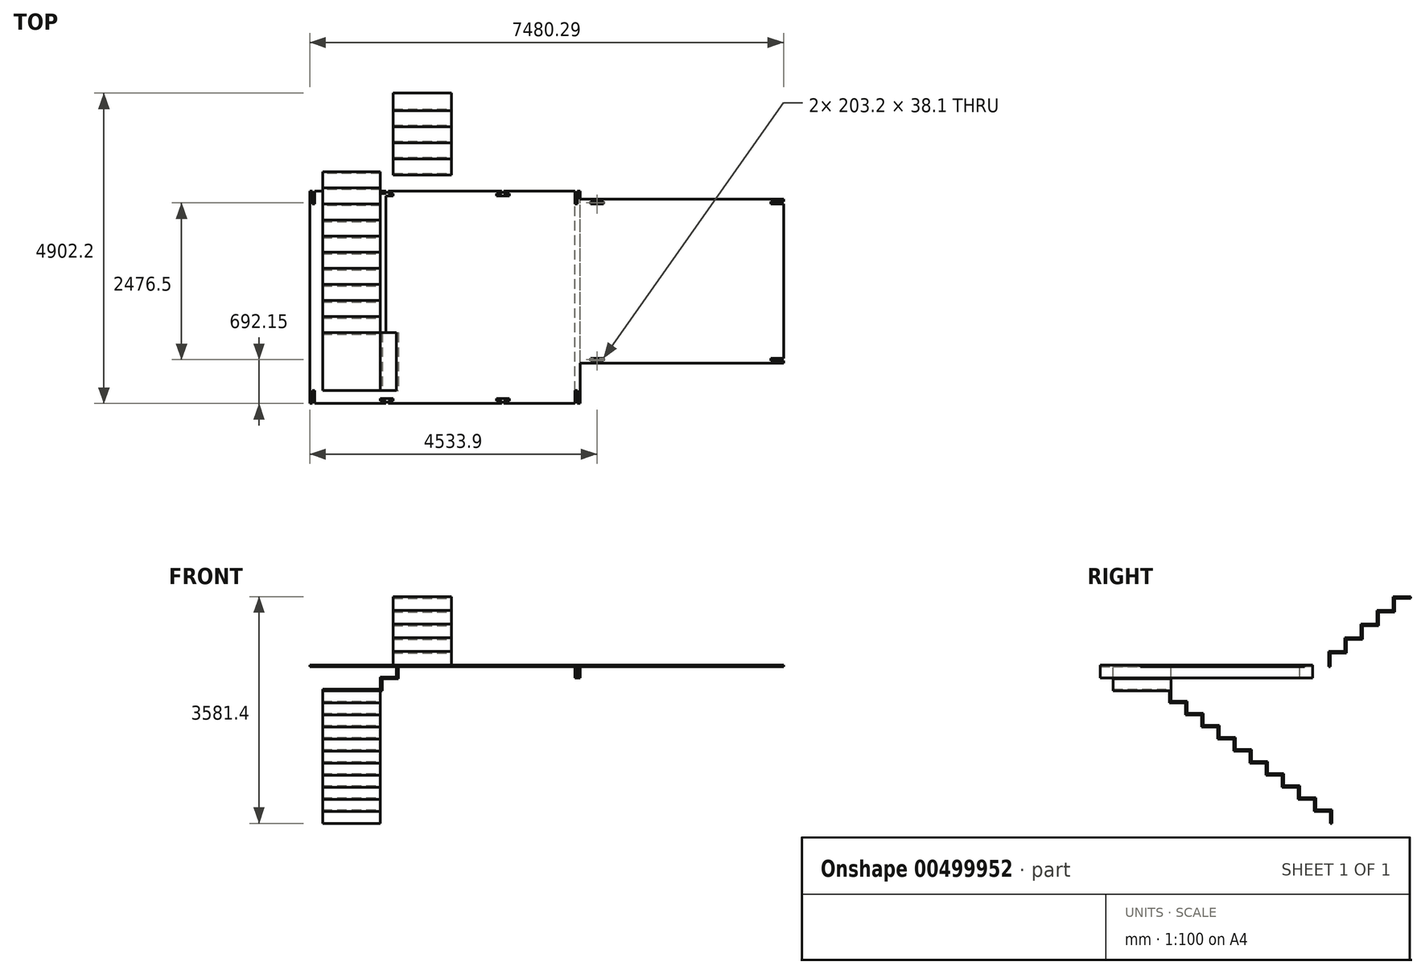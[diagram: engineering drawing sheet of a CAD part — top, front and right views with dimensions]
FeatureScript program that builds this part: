
annotation { "Feature Type Name" : "Feature", "Feature Type Description" : "" }
export const myFeature = defineFeature(function(context is Context, id is Id, definition is map)
    precondition{}
    {
        {
            var Q0;
            Q0=qCreatedBy(makeId("Top.planeOp"),FACE);
            var sketch = newSketch(context, id + "F0", { "sketchPlane" : qUnion([Q0])});
            skLineSegment(sketch, "E0.bottom", {"start": v(-4114.17, 1676.4) * mm, "end": v(4114.16, 1676.4) * mm});
            skLineSegment(sketch, "E0.top", {"start": v(-4114.17, -1676.4) * mm, "end": v(4114.17, -1676.4) * mm});
            skLineSegment(sketch, "E0.left", {"start": v(-4114.17, 1676.4) * mm, "end": v(-4114.17, -1676.4) * mm});
            skPoint(sketch, "E0.middle", {"position": v(0, 0) * mm});
            skLineSegment(sketch, "E1.bottom", {"start": v(-4076.07, -1676.4) * mm, "end": v(-4037.97, -1676.4) * mm});
            skLineSegment(sketch, "E1.top", {"start": v(-4076.07, -1473.2) * mm, "end": v(-4037.97, -1473.2) * mm});
            skLineSegment(sketch, "E1.left", {"start": v(-4076.07, -1676.4) * mm, "end": v(-4076.07, -1473.2) * mm});
            skLineSegment(sketch, "E1.right", {"start": v(-4037.97, -1676.4) * mm, "end": v(-4037.97, -1473.2) * mm});
            skLineSegment(sketch, "E2.bottom", {"start": v(-2914.02, -1676.4) * mm, "end": v(-2875.92, -1676.4) * mm});
            skLineSegment(sketch, "E2.top", {"start": v(-2914.02, -1473.2) * mm, "end": v(-2875.92, -1473.2) * mm});
            skLineSegment(sketch, "E2.left", {"start": v(-2914.02, -1676.4) * mm, "end": v(-2914.02, -1473.2) * mm});
            skLineSegment(sketch, "E2.right", {"start": v(-2875.92, -1676.4) * mm, "end": v(-2875.92, -1473.2) * mm});
            skLineSegment(sketch, "E3.bottom", {"start": v(-1085.22, -1676.4) * mm, "end": v(-1047.12, -1676.4) * mm});
            skLineSegment(sketch, "E3.top", {"start": v(-1085.22, -1473.2) * mm, "end": v(-1047.12, -1473.2) * mm});
            skLineSegment(sketch, "E3.left", {"start": v(-1085.22, -1676.4) * mm, "end": v(-1085.22, -1473.2) * mm});
            skLineSegment(sketch, "E3.right", {"start": v(-1047.12, -1676.4) * mm, "end": v(-1047.12, -1473.2) * mm});
            skLineSegment(sketch, "E4.bottom", {"start": v(76.84, -1676.4) * mm, "end": v(114.94, -1676.4) * mm});
            skLineSegment(sketch, "E4.top", {"start": v(76.84, -1473.2) * mm, "end": v(114.94, -1473.2) * mm});
            skLineSegment(sketch, "E4.left", {"start": v(76.84, -1676.4) * mm, "end": v(76.84, -1473.2) * mm});
            skLineSegment(sketch, "E4.right", {"start": v(114.94, -1676.4) * mm, "end": v(114.94, -1473.2) * mm});
            skLineSegment(sketch, "E5.bottom", {"start": v(-4076.07, 1676.4) * mm, "end": v(-4037.97, 1676.4) * mm});
            skLineSegment(sketch, "E5.top", {"start": v(-4076.07, 1473.2) * mm, "end": v(-4037.97, 1473.2) * mm});
            skLineSegment(sketch, "E5.left", {"start": v(-4076.07, 1676.4) * mm, "end": v(-4076.07, 1473.2) * mm});
            skLineSegment(sketch, "E5.right", {"start": v(-4037.97, 1676.4) * mm, "end": v(-4037.97, 1473.2) * mm});
            skLineSegment(sketch, "E6.bottom", {"start": v(-2914.02, 1676.4) * mm, "end": v(-2875.92, 1676.4) * mm});
            skLineSegment(sketch, "E6.top", {"start": v(-2914.02, 1473.2) * mm, "end": v(-2875.92, 1473.2) * mm});
            skLineSegment(sketch, "E6.left", {"start": v(-2914.02, 1676.4) * mm, "end": v(-2914.02, 1473.2) * mm});
            skLineSegment(sketch, "E6.right", {"start": v(-2875.92, 1676.4) * mm, "end": v(-2875.92, 1473.2) * mm});
            skLineSegment(sketch, "E7.bottom", {"start": v(-1085.22, 1676.4) * mm, "end": v(-1047.12, 1676.4) * mm});
            skLineSegment(sketch, "E7.top", {"start": v(-1085.22, 1473.2) * mm, "end": v(-1047.12, 1473.2) * mm});
            skLineSegment(sketch, "E7.left", {"start": v(-1085.22, 1676.4) * mm, "end": v(-1085.22, 1473.2) * mm});
            skLineSegment(sketch, "E7.right", {"start": v(-1047.12, 1676.4) * mm, "end": v(-1047.12, 1473.2) * mm});
            skLineSegment(sketch, "E8.bottom", {"start": v(76.84, 1676.4) * mm, "end": v(114.94, 1676.4) * mm});
            skLineSegment(sketch, "E8.top", {"start": v(76.84, 1473.2) * mm, "end": v(114.94, 1473.2) * mm});
            skLineSegment(sketch, "E8.left", {"start": v(76.84, 1676.4) * mm, "end": v(76.84, 1473.2) * mm});
            skLineSegment(sketch, "E8.right", {"start": v(114.94, 1676.4) * mm, "end": v(114.94, 1473.2) * mm});
            skLineSegment(sketch, "E9.bottom", {"start": v(76.84, -1676.4) * mm, "end": v(153.04, -1676.4) * mm});
            skLineSegment(sketch, "E9.top", {"start": v(76.84, 1676.4) * mm, "end": v(153.04, 1676.4) * mm});
            skLineSegment(sketch, "E9.left", {"start": v(76.84, -1676.4) * mm, "end": v(76.84, 1676.4) * mm});
            skLineSegment(sketch, "E9.right", {"start": v(153.04, -1676.4) * mm, "end": v(153.04, 1676.4) * mm});
            skLineSegment(sketch, "E10", {"start": v(-4076.07, -1638.3) * mm, "end": v(-4037.97, -1638.3) * mm});
            skLineSegment(sketch, "E11", {"start": v(-4076.07, 1638.3) * mm, "end": v(-4037.97, 1638.3) * mm});
            skLineSegment(sketch, "E12", {"start": v(76.84, -1638.3) * mm, "end": v(114.94, -1638.3) * mm});
            skLineSegment(sketch, "E13.bottom", {"start": v(-1167.77, -1638.3) * mm, "end": v(-964.57, -1638.3) * mm});
            skLineSegment(sketch, "E13.top", {"start": v(-1167.77, -1600.2) * mm, "end": v(-964.57, -1600.2) * mm});
            skLineSegment(sketch, "E13.left", {"start": v(-1167.77, -1638.3) * mm, "end": v(-1167.77, -1600.2) * mm});
            skLineSegment(sketch, "E13.right", {"start": v(-964.57, -1638.3) * mm, "end": v(-964.57, -1600.2) * mm});
            skLineSegment(sketch, "E14.bottom", {"start": v(-2996.57, 1676.4) * mm, "end": v(-3910.97, 1676.4) * mm});
            skLineSegment(sketch, "E14.top", {"start": v(-2996.57, -1473.2) * mm, "end": v(-3910.96, -1473.2) * mm});
            skLineSegment(sketch, "E14.left", {"start": v(-2996.57, 1676.4) * mm, "end": v(-2996.57, -1473.2) * mm});
            skLineSegment(sketch, "E14.right", {"start": v(-3910.97, 1676.4) * mm, "end": v(-3910.96, -1473.2) * mm});
            skPoint(sketch, "E15.oppositeSnap0", {"position": v(-2875.92, -1574.8) * mm});
            skLineSegment(sketch, "E15.bottom", {"start": v(-2996.57, -1638.3) * mm, "end": v(-2793.37, -1638.3) * mm});
            skLineSegment(sketch, "E15.top", {"start": v(-2996.57, -1600.2) * mm, "end": v(-2793.37, -1600.2) * mm});
            skLineSegment(sketch, "E15.left", {"start": v(-2996.57, -1638.3) * mm, "end": v(-2996.57, -1600.2) * mm});
            skLineSegment(sketch, "E15.right", {"start": v(-2793.37, -1638.3) * mm, "end": v(-2793.37, -1600.2) * mm});
            skLineSegment(sketch, "E16.bottom", {"start": v(-2996.57, 1638.3) * mm, "end": v(-2793.37, 1638.3) * mm});
            skLineSegment(sketch, "E16.top", {"start": v(-2996.57, 1600.2) * mm, "end": v(-2793.37, 1600.2) * mm});
            skLineSegment(sketch, "E16.left", {"start": v(-2996.57, 1638.3) * mm, "end": v(-2996.57, 1600.2) * mm});
            skLineSegment(sketch, "E16.right", {"start": v(-2793.37, 1638.3) * mm, "end": v(-2793.37, 1600.2) * mm});
            skLineSegment(sketch, "E17.bottom", {"start": v(-1167.77, 1638.3) * mm, "end": v(-964.57, 1638.3) * mm});
            skLineSegment(sketch, "E17.top", {"start": v(-1167.77, 1600.2) * mm, "end": v(-964.57, 1600.2) * mm});
            skLineSegment(sketch, "E17.left", {"start": v(-1167.77, 1638.3) * mm, "end": v(-1167.77, 1600.2) * mm});
            skLineSegment(sketch, "E17.right", {"start": v(-964.57, 1638.3) * mm, "end": v(-964.57, 1600.2) * mm});
            skLineSegment(sketch, "E18.bottom", {"start": v(-2996.57, -1473.2) * mm, "end": v(-2742.57, -1473.2) * mm});
            skLineSegment(sketch, "E18.top", {"start": v(-2996.57, -558.8) * mm, "end": v(-2742.56, -558.8) * mm});
            skLineSegment(sketch, "E18.left", {"start": v(-2996.57, -1473.2) * mm, "end": v(-2996.57, -558.8) * mm});
            skLineSegment(sketch, "E18.right", {"start": v(-2742.57, -1473.2) * mm, "end": v(-2742.57, -558.8) * mm});
            skLineSegment(sketch, "E19.bottom", {"start": v(-2742.56, -558.8) * mm, "end": v(-2717.16, -558.8) * mm});
            skLineSegment(sketch, "E19.top", {"start": v(-2742.57, -1473.2) * mm, "end": v(-2717.17, -1473.2) * mm});
            skLineSegment(sketch, "E19.left", {"start": v(-2742.57, -558.8) * mm, "end": v(-2742.57, -1473.2) * mm});
            skLineSegment(sketch, "E19.right", {"start": v(-2717.17, -558.8) * mm, "end": v(-2717.17, -1473.2) * mm});
            skLineSegment(sketch, "E20.bottom", {"start": v(-2996.57, -558.8) * mm, "end": v(-2914.02, -558.8) * mm});
            skLineSegment(sketch, "E20.top", {"start": v(-2996.57, 1676.4) * mm, "end": v(-2914.02, 1676.4) * mm});
            skLineSegment(sketch, "E20.left", {"start": v(-2996.57, -558.8) * mm, "end": v(-2996.57, 1676.4) * mm});
            skLineSegment(sketch, "E20.right", {"start": v(-2914.02, -558.8) * mm, "end": v(-2914.02, 1676.4) * mm});
            skLineSegment(sketch, "E21.bottom", {"start": v(-2793.37, 1676.4) * mm, "end": v(-1878.97, 1676.4) * mm});
            skLineSegment(sketch, "E21.top", {"start": v(-2793.37, 1955.8) * mm, "end": v(-1878.97, 1955.8) * mm});
            skLineSegment(sketch, "E21.left", {"start": v(-2793.37, 1676.4) * mm, "end": v(-2793.37, 1955.8) * mm});
            skLineSegment(sketch, "E21.right", {"start": v(-1878.97, 1676.4) * mm, "end": v(-1878.97, 1955.8) * mm});
            skLineSegment(sketch, "E22.bottom", {"start": v(153.04, 1549.4) * mm, "end": v(3366.14, 1549.4) * mm});
            skLineSegment(sketch, "E22.top", {"start": v(153.04, -1041.4) * mm, "end": v(3366.13, -1041.4) * mm});
            skLineSegment(sketch, "E22.left", {"start": v(153.04, 1549.4) * mm, "end": v(153.04, -1041.4) * mm});
            skLineSegment(sketch, "E22.right", {"start": v(3366.14, 1549.4) * mm, "end": v(3366.14, -1041.4) * mm});
            skLineSegment(sketch, "E23.bottom", {"start": v(318.14, 1511.3) * mm, "end": v(521.34, 1511.3) * mm});
            skLineSegment(sketch, "E23.top", {"start": v(318.14, 1473.2) * mm, "end": v(521.34, 1473.2) * mm});
            skLineSegment(sketch, "E23.left", {"start": v(318.14, 1511.3) * mm, "end": v(318.14, 1473.2) * mm});
            skLineSegment(sketch, "E23.right", {"start": v(521.34, 1511.3) * mm, "end": v(521.34, 1473.2) * mm});
            skLineSegment(sketch, "E24.bottom", {"start": v(318.14, -965.2) * mm, "end": v(521.34, -965.2) * mm});
            skLineSegment(sketch, "E24.top", {"start": v(318.14, -1003.3) * mm, "end": v(521.34, -1003.3) * mm});
            skLineSegment(sketch, "E24.left", {"start": v(318.14, -965.2) * mm, "end": v(318.14, -1003.3) * mm});
            skLineSegment(sketch, "E24.right", {"start": v(521.34, -965.2) * mm, "end": v(521.34, -1003.3) * mm});
            skLineSegment(sketch, "E25.bottom", {"start": v(3366.14, -965.2) * mm, "end": v(3162.94, -965.2) * mm});
            skLineSegment(sketch, "E25.top", {"start": v(3366.14, -1003.3) * mm, "end": v(3162.94, -1003.3) * mm});
            skLineSegment(sketch, "E25.left", {"start": v(3366.14, -965.2) * mm, "end": v(3366.14, -1003.3) * mm});
            skLineSegment(sketch, "E25.right", {"start": v(3162.94, -965.2) * mm, "end": v(3162.94, -1003.3) * mm});
            skLineSegment(sketch, "E26.bottom", {"start": v(3366.14, 1511.3) * mm, "end": v(3162.94, 1511.3) * mm});
            skLineSegment(sketch, "E26.top", {"start": v(3366.14, 1473.2) * mm, "end": v(3162.94, 1473.2) * mm});
            skLineSegment(sketch, "E26.left", {"start": v(3366.14, 1511.3) * mm, "end": v(3366.14, 1473.2) * mm});
            skLineSegment(sketch, "E26.right", {"start": v(3162.94, 1511.3) * mm, "end": v(3162.94, 1473.2) * mm});
            skSolve(sketch);
        }
        {
            var Q0;
            Q0=makeQuery(id+"F0.imprint","IMPRINT",FACE,{"disambiguationData":[TD([[makeQuery(id+"F0.imprint","IMPRINT",EDGE,{"derivedFrom":sQuery(id+"F0.wireOp",EDGE,"E1.bottom")}),1.0]])]});
            var Q1;
            Q1=makeQuery(id+"F0.imprint","IMPRINT",FACE,{"disambiguationData":[TD([[makeQuery(id+"F0.imprint","IMPRINT",EDGE,{"derivedFrom":sQuery(id+"F0.wireOp",EDGE,"E2.bottom")}),1.0]])]});
            var Q2;
            Q2=makeQuery(id+"F0.imprint","IMPRINT",FACE,{"disambiguationData":[TD([[makeQuery(id+"F0.imprint","IMPRINT",EDGE,{"derivedFrom":sQuery(id+"F0.wireOp",EDGE,"E3.bottom")}),1.0]])]});
            var Q3;
            Q3=makeQuery(id+"F0.imprint","IMPRINT",FACE,{"disambiguationData":[TD([[makeQuery(id+"F0.imprint","IMPRINT",EDGE,{"derivedFrom":sQuery(id+"F0.wireOp",EDGE,"E4.bottom")}),1.0]])]});
            var Q4;
            Q4=makeQuery(id+"F0.imprint","IMPRINT",FACE,{"disambiguationData":[TD([[makeQuery(id+"F0.imprint","IMPRINT",EDGE,{"derivedFrom":sQuery(id+"F0.wireOp",EDGE,"E5.bottom")}),-1.0]])]});
            var Q5;
            Q5=makeQuery(id+"F0.imprint","IMPRINT",FACE,{"disambiguationData":[TD([[makeQuery(id+"F0.imprint","IMPRINT",EDGE,{"derivedFrom":sQuery(id+"F0.wireOp",EDGE,"E6.bottom")}),-1.0]])]});
            var Q6;
            Q6=makeQuery(id+"F0.imprint","IMPRINT",FACE,{"disambiguationData":[TD([[makeQuery(id+"F0.imprint","IMPRINT",EDGE,{"derivedFrom":sQuery(id+"F0.wireOp",EDGE,"E7.bottom")}),-1.0]])]});
            var Q7;
            Q7=makeQuery(id+"F0.imprint","IMPRINT",FACE,{"disambiguationData":[TD([[makeQuery(id+"F0.imprint","IMPRINT",EDGE,{"derivedFrom":sQuery(id+"F0.wireOp",EDGE,"E8.bottom")}),-1.0]])]});
            var Q8;
            {var subQ4=sQuery(id+"F0.wireOp",EDGE,"E0.left");Q8=makeQuery(id+"F0.imprint","IMPRINT",FACE,{"disambiguationData":[TD([[makeQuery(id+"F0.imprint","IMPRINT",EDGE,{"derivedFrom":subQ4}),1.0]])]});}
            var Q9;
            Q9=makeQuery(id+"F0.imprint","IMPRINT",FACE,{"disambiguationData":[TD([[makeQuery(id+"F0.imprint","IMPRINT",EDGE,{"derivedFrom":sQuery(id+"F0.wireOp",EDGE,"E9.bottom")}),1.0]])]});
            var Q10;
            {var subQ0=sQuery(id+"F0.wireOp",EDGE,"E3.top");Q10=makeQuery(id+"F0.imprint","IMPRINT",FACE,{"disambiguationData":[TD([[makeQuery(id+"F0.imprint","IMPRINT",EDGE,{"derivedFrom":subQ0}),-1.0]])]});}
            var Q11;
            {var subQ2=sQuery(id+"F0.wireOp",EDGE,"E4.top");Q11=makeQuery(id+"F0.imprint","IMPRINT",FACE,{"disambiguationData":[TD([[makeQuery(id+"F0.imprint","IMPRINT",EDGE,{"derivedFrom":subQ2}),1.0]])]});}
            var Q12;
            {var subQ0=sQuery(id+"F0.wireOp",EDGE,"E7.top");Q12=makeQuery(id+"F0.imprint","IMPRINT",FACE,{"disambiguationData":[TD([[makeQuery(id+"F0.imprint","IMPRINT",EDGE,{"derivedFrom":subQ0}),1.0]])]});}
            var Q13;
            {var subQ0=sQuery(id+"F0.wireOp",EDGE,"E6.top");Q13=makeQuery(id+"F0.imprint","IMPRINT",FACE,{"disambiguationData":[TD([[makeQuery(id+"F0.imprint","IMPRINT",EDGE,{"derivedFrom":subQ0}),1.0]])]});}
            var Q14;
            {var subQ0=sQuery(id+"F0.wireOp",EDGE,"E2.top");Q14=makeQuery(id+"F0.imprint","IMPRINT",FACE,{"disambiguationData":[TD([[makeQuery(id+"F0.imprint","IMPRINT",EDGE,{"derivedFrom":subQ0}),-1.0]])]});}
            var Q15;
            {var subQ0=sQuery(id+"F0.wireOp",EDGE,"E6.left");var subQ5=sQuery(id+"F0.wireOp",EDGE,"E16.bottom");var subQ7=makeQuery(id+"F0.imprint","INTERSECT",VERTEX,{"derivedFrom":[subQ0,subQ5]});Q15=makeQuery(id+"F0.imprint","IMPRINT",FACE,{"disambiguationData":[TD([[makeQuery(id+"F0.imprint","IMPRINT",EDGE,{"disambiguationData":[TD([[subQ7,1.0]])],"derivedFrom":subQ0}),-1.0]])]});}
            var Q16;
            {var subQ38=sQuery(id+"F0.wireOp",EDGE,"E3.top");Q16=makeQuery(id+"F0.imprint","IMPRINT",FACE,{"disambiguationData":[TD([[makeQuery(id+"F0.imprint","IMPRINT",EDGE,{"derivedFrom":subQ38}),1.0]])]});}
            var Q17;
            {var subQ0=sQuery(id+"F0.wireOp",EDGE,"E18.bottom");var subQ1=sQuery(id+"F0.wireOp",EDGE,"E2.left");var subQ2=makeQuery(id+"F0.imprint","INTERSECT",VERTEX,{"derivedFrom":[subQ1,subQ0]});Q17=makeQuery(id+"F0.imprint","IMPRINT",FACE,{"disambiguationData":[TD([[makeQuery(id+"F0.imprint","IMPRINT",EDGE,{"disambiguationData":[TD([[subQ2,1.0]])],"derivedFrom":subQ1}),-1.0]])]});}
            var Q18;
            Q18=makeQuery(id+"F0.imprint","IMPRINT",FACE,{"disambiguationData":[TD([[makeQuery(id+"F0.imprint","IMPRINT",EDGE,{"derivedFrom":sQuery(id+"F0.wireOp",EDGE,"E19.bottom")}),-1.0]])]});
            var Q19;
            {var subQ3=sQuery(id+"F0.wireOp",EDGE,"E20.bottom");Q19=makeQuery(id+"F0.imprint","IMPRINT",FACE,{"disambiguationData":[TD([[makeQuery(id+"F0.imprint","IMPRINT",EDGE,{"derivedFrom":subQ3}),1.0]])]});}
            var Q20;
            {var subQ5=sQuery(id+"F0.wireOp",EDGE,"E20.top");Q20=makeQuery(id+"F0.imprint","IMPRINT",FACE,{"disambiguationData":[TD([[makeQuery(id+"F0.imprint","IMPRINT",EDGE,{"derivedFrom":subQ5}),-1.0]])]});}
            var Q21;
            Q21=makeQuery(id+"F0.imprint","IMPRINT",FACE,{"disambiguationData":[TD([[makeQuery(id+"F0.imprint","IMPRINT",EDGE,{"derivedFrom":sQuery(id+"F0.wireOp",EDGE,"E21.bottom")}),1.0]])]});
            var Q22;
            Q22=makeQuery(id+"F0.imprint","IMPRINT",FACE,{"disambiguationData":[TD([[makeQuery(id+"F0.imprint","IMPRINT",EDGE,{"derivedFrom":sQuery(id+"F0.wireOp",EDGE,"E22.bottom")}),-1.0]])]});
            extrude(context, id + "F1", {"entities" : qUnion([Q0, Q1, Q2, Q3, Q4, Q5, Q6, Q7, Q8, Q9, Q10, Q11, Q12, Q13, Q14, Q15, Q16, Q17, Q18, Q19, Q20, Q21, Q22]), "oppositeDirection" : true, "depth" : 25.4 * mm, "offsetDistance" : 25.4 * mm});
        }
        {
            var Q0;
            {var subQ1=sQuery(id+"F0.wireOp",EDGE,"E8.top");Q0=makeQuery(id+"F0.imprint","IMPRINT",FACE,{"disambiguationData":[TD([[makeQuery(id+"F0.imprint","IMPRINT",EDGE,{"derivedFrom":subQ1}),-1.0]])]});}
            extrude(context, id + "F2", {"entities" : qUnion([Q0]), "operationType" : NewBodyOperationType.ADD, "oppositeDirection" : true, "depth" : 203.2 * mm, "offsetDistance" : 25.4 * mm});
        }
        {
            var Q0;
            Q0=makeQuery(id+"F0.imprint","IMPRINT",FACE,{"disambiguationData":[TD([[makeQuery(id+"F0.imprint","IMPRINT",EDGE,{"derivedFrom":sQuery(id+"F0.wireOp",EDGE,"E19.bottom")}),-1.0]])]});
            extrude(context, id + "F3", {"entities" : qUnion([Q0]), "operationType" : NewBodyOperationType.ADD, "oppositeDirection" : true, "depth" : 215.9 * mm, "offsetDistance" : 25.4 * mm});
        }
        {
            var Q0;
            Q0=makeQuery(id+"F3.opExtrude","SWEPT_FACE",FACE,{"disambiguationData":[OSD([sQuery(id+"F0.wireOp",EDGE,"E19.right")])]});
            var sketch = newSketch(context, id + "F4", { "sketchPlane" : qUnion([Q0])});
            skLineSegment(sketch, "E27.bottom", {"start": v(-1473.2, -215.9) * mm, "end": v(-558.8, -215.9) * mm});
            skLineSegment(sketch, "E27.top", {"start": v(-1473.2, -190.5) * mm, "end": v(-558.8, -190.5) * mm});
            skLineSegment(sketch, "E27.left", {"start": v(-1473.2, -215.9) * mm, "end": v(-1473.2, -190.5) * mm});
            skLineSegment(sketch, "E27.right", {"start": v(-558.8, -215.9) * mm, "end": v(-558.8, -190.5) * mm});
            skSolve(sketch);
        }
        {
            var Q0;
            Q0 = qSketchRegion(id + "F4", true);
            extrude(context, id + "F5", {"entities" : qUnion([Q0]), "operationType" : NewBodyOperationType.ADD, "oppositeDirection" : true, "depth" : 279.4 * mm, "offsetDistance" : 25.4 * mm});
        }
        {
            var Q0;
            Q0=makeQuery(id+"F5.opExtrude","SWEPT_FACE",FACE,{"disambiguationData":[OSD([sQuery(id+"F4.wireOp",EDGE,"E27.top")])]});
            var sketch = newSketch(context, id + "F6", { "sketchPlane" : qUnion([Q0])});
            skLineSegment(sketch, "E28.bottom", {"start": v(-2996.57, -558.8) * mm, "end": v(-2971.17, -558.8) * mm});
            skLineSegment(sketch, "E28.top", {"start": v(-2996.57, -1473.2) * mm, "end": v(-2971.17, -1473.2) * mm});
            skLineSegment(sketch, "E28.left", {"start": v(-2996.57, -558.8) * mm, "end": v(-2996.57, -1473.2) * mm});
            skLineSegment(sketch, "E28.right", {"start": v(-2971.17, -558.8) * mm, "end": v(-2971.17, -1473.2) * mm});
            skSolve(sketch);
        }
        {
            var Q0;
            Q0 = qSketchRegion(id + "F6", true);
            extrude(context, id + "F7", {"entities" : qUnion([Q0]), "operationType" : NewBodyOperationType.ADD, "oppositeDirection" : true, "depth" : 215.9 * mm, "offsetDistance" : 25.4 * mm});
        }
        {
            var Q0;
            Q0=makeQuery(id+"F7.opExtrude","SWEPT_FACE",FACE,{"disambiguationData":[OSD([sQuery(id+"F6.wireOp",EDGE,"E28.right")])]});
            var sketch = newSketch(context, id + "F8", { "sketchPlane" : qUnion([Q0])});
            skLineSegment(sketch, "E29.bottom", {"start": v(-1473.2, -406.4) * mm, "end": v(-558.8, -406.4) * mm});
            skLineSegment(sketch, "E29.top", {"start": v(-1473.2, -381) * mm, "end": v(-558.8, -381) * mm});
            skLineSegment(sketch, "E29.left", {"start": v(-1473.2, -406.4) * mm, "end": v(-1473.2, -381) * mm});
            skLineSegment(sketch, "E29.right", {"start": v(-558.8, -406.4) * mm, "end": v(-558.8, -381) * mm});
            skSolve(sketch);
        }
        {
            var Q0;
            Q0 = qSketchRegion(id + "F8", true);
            extrude(context, id + "F9", {"entities" : qUnion([Q0]), "operationType" : NewBodyOperationType.ADD, "oppositeDirection" : true, "depth" : 939.8 * mm, "offsetDistance" : 25.4 * mm});
        }
        {
            var Q0;
            Q0=makeQuery(id+"F9.opExtrude","SWEPT_FACE",FACE,{"disambiguationData":[OSD([sQuery(id+"F8.wireOp",EDGE,"E29.top")])]});
            var sketch = newSketch(context, id + "F10", { "sketchPlane" : qUnion([Q0])});
            skLineSegment(sketch, "E30.bottom", {"start": v(-3910.97, -558.8) * mm, "end": v(-2996.57, -558.8) * mm});
            skLineSegment(sketch, "E30.top", {"start": v(-3910.97, -584.2) * mm, "end": v(-2996.57, -584.2) * mm});
            skLineSegment(sketch, "E30.left", {"start": v(-3910.97, -558.8) * mm, "end": v(-3910.97, -584.2) * mm});
            skLineSegment(sketch, "E30.right", {"start": v(-2996.57, -558.8) * mm, "end": v(-2996.57, -584.2) * mm});
            skSolve(sketch);
        }
        {
            var Q0;
            Q0 = qSketchRegion(id + "F10", true);
            extrude(context, id + "F11", {"entities" : qUnion([Q0]), "operationType" : NewBodyOperationType.ADD, "oppositeDirection" : true, "depth" : 215.9 * mm, "offsetDistance" : 25.4 * mm});
        }
        {
            var Q0;
            Q0=makeQuery(id+"F11.opExtrude","SWEPT_FACE",FACE,{"disambiguationData":[OSD([sQuery(id+"F10.wireOp",EDGE,"E30.top")])]});
            var sketch = newSketch(context, id + "F12", { "sketchPlane" : qUnion([Q0])});
            skLineSegment(sketch, "E31.bottom", {"start": v(-3910.97, -596.9) * mm, "end": v(-2996.57, -596.9) * mm});
            skLineSegment(sketch, "E31.top", {"start": v(-3910.97, -571.5) * mm, "end": v(-2996.57, -571.5) * mm});
            skLineSegment(sketch, "E31.left", {"start": v(-3910.97, -596.9) * mm, "end": v(-3910.97, -571.5) * mm});
            skLineSegment(sketch, "E31.right", {"start": v(-2996.57, -596.9) * mm, "end": v(-2996.57, -571.5) * mm});
            skSolve(sketch);
        }
        {
            var Q0;
            Q0 = qSketchRegion(id + "F12", true);
            extrude(context, id + "F13", {"entities" : qUnion([Q0]), "operationType" : NewBodyOperationType.ADD, "oppositeDirection" : true, "depth" : 279.4 * mm, "offsetDistance" : 25.4 * mm});
        }
        {
            var Q0;
            Q0=makeQuery(id+"F13.opExtrude","SWEPT_FACE",FACE,{"disambiguationData":[OSD([sQuery(id+"F12.wireOp",EDGE,"E31.top")])]});
            var sketch = newSketch(context, id + "F14", { "sketchPlane" : qUnion([Q0])});
            skLineSegment(sketch, "E32.bottom", {"start": v(-3910.97, -304.8) * mm, "end": v(-2996.57, -304.8) * mm});
            skLineSegment(sketch, "E32.top", {"start": v(-3910.97, -330.2) * mm, "end": v(-2996.57, -330.2) * mm});
            skLineSegment(sketch, "E32.left", {"start": v(-3910.97, -304.8) * mm, "end": v(-3910.97, -330.2) * mm});
            skLineSegment(sketch, "E32.right", {"start": v(-2996.57, -304.8) * mm, "end": v(-2996.57, -330.2) * mm});
            skSolve(sketch);
        }
        {
            var Q0;
            Q0 = qSketchRegion(id + "F14", true);
            extrude(context, id + "F15", {"entities" : qUnion([Q0]), "operationType" : NewBodyOperationType.ADD, "oppositeDirection" : true, "depth" : 215.9 * mm, "offsetDistance" : 25.4 * mm});
        }
        {
            var Q0;
            Q0=makeQuery(id+"F15.opExtrude","SWEPT_FACE",FACE,{"disambiguationData":[OSD([sQuery(id+"F14.wireOp",EDGE,"E32.top")])]});
            var sketch = newSketch(context, id + "F16", { "sketchPlane" : qUnion([Q0])});
            skLineSegment(sketch, "E33.bottom", {"start": v(-3910.97, -787.4) * mm, "end": v(-2996.57, -787.4) * mm});
            skLineSegment(sketch, "E33.top", {"start": v(-3910.97, -762) * mm, "end": v(-2996.57, -762) * mm});
            skLineSegment(sketch, "E33.left", {"start": v(-3910.97, -787.4) * mm, "end": v(-3910.97, -762) * mm});
            skLineSegment(sketch, "E33.right", {"start": v(-2996.57, -787.4) * mm, "end": v(-2996.57, -762) * mm});
            skSolve(sketch);
        }
        {
            var Q0;
            Q0 = qSketchRegion(id + "F16", true);
            extrude(context, id + "F17", {"entities" : qUnion([Q0]), "operationType" : NewBodyOperationType.ADD, "oppositeDirection" : true, "depth" : 279.4 * mm, "offsetDistance" : 25.4 * mm});
        }
        {
            var Q0;
            Q0=makeQuery(id+"F17.opExtrude","SWEPT_FACE",FACE,{"disambiguationData":[OSD([sQuery(id+"F16.wireOp",EDGE,"E33.top")])]});
            var sketch = newSketch(context, id + "F18", { "sketchPlane" : qUnion([Q0])});
            skLineSegment(sketch, "E34.bottom", {"start": v(-3910.97, -50.8) * mm, "end": v(-2996.57, -50.8) * mm});
            skLineSegment(sketch, "E34.top", {"start": v(-3910.97, -76.2) * mm, "end": v(-2996.57, -76.2) * mm});
            skLineSegment(sketch, "E34.left", {"start": v(-3910.97, -50.8) * mm, "end": v(-3910.97, -76.2) * mm});
            skLineSegment(sketch, "E34.right", {"start": v(-2996.57, -50.8) * mm, "end": v(-2996.57, -76.2) * mm});
            skSolve(sketch);
        }
        {
            var Q0;
            Q0 = qSketchRegion(id + "F18", true);
            extrude(context, id + "F19", {"entities" : qUnion([Q0]), "operationType" : NewBodyOperationType.ADD, "oppositeDirection" : true, "depth" : 215.9 * mm, "offsetDistance" : 25.4 * mm});
        }
        {
            var Q0;
            Q0=makeQuery(id+"F19.opExtrude","SWEPT_FACE",FACE,{"disambiguationData":[OSD([sQuery(id+"F18.wireOp",EDGE,"E34.top")])]});
            var sketch = newSketch(context, id + "F20", { "sketchPlane" : qUnion([Q0])});
            skLineSegment(sketch, "E35.bottom", {"start": v(-3910.97, -977.9) * mm, "end": v(-2996.57, -977.9) * mm});
            skLineSegment(sketch, "E35.top", {"start": v(-3910.97, -952.5) * mm, "end": v(-2996.57, -952.5) * mm});
            skLineSegment(sketch, "E35.left", {"start": v(-3910.97, -977.9) * mm, "end": v(-3910.97, -952.5) * mm});
            skLineSegment(sketch, "E35.right", {"start": v(-2996.57, -977.9) * mm, "end": v(-2996.57, -952.5) * mm});
            skSolve(sketch);
        }
        {
            var Q0;
            Q0 = qSketchRegion(id + "F20", true);
            extrude(context, id + "F21", {"entities" : qUnion([Q0]), "operationType" : NewBodyOperationType.ADD, "oppositeDirection" : true, "depth" : 279.4 * mm, "offsetDistance" : 25.4 * mm});
        }
        {
            var Q0;
            Q0=makeQuery(id+"F21.opExtrude","SWEPT_FACE",FACE,{"disambiguationData":[OSD([sQuery(id+"F20.wireOp",EDGE,"E35.top")])]});
            var sketch = newSketch(context, id + "F22", { "sketchPlane" : qUnion([Q0])});
            skLineSegment(sketch, "E36.bottom", {"start": v(-3910.97, 203.2) * mm, "end": v(-2996.57, 203.2) * mm});
            skLineSegment(sketch, "E36.top", {"start": v(-3910.97, 177.8) * mm, "end": v(-2996.57, 177.8) * mm});
            skLineSegment(sketch, "E36.left", {"start": v(-3910.97, 203.2) * mm, "end": v(-3910.97, 177.8) * mm});
            skLineSegment(sketch, "E36.right", {"start": v(-2996.57, 203.2) * mm, "end": v(-2996.57, 177.8) * mm});
            skSolve(sketch);
        }
        {
            var Q0;
            Q0 = qSketchRegion(id + "F22", true);
            extrude(context, id + "F23", {"entities" : qUnion([Q0]), "operationType" : NewBodyOperationType.ADD, "oppositeDirection" : true, "depth" : 215.9 * mm, "offsetDistance" : 25.4 * mm});
        }
        {
            var Q0;
            Q0=makeQuery(id+"F23.opExtrude","SWEPT_FACE",FACE,{"disambiguationData":[OSD([sQuery(id+"F22.wireOp",EDGE,"E36.top")])]});
            var sketch = newSketch(context, id + "F24", { "sketchPlane" : qUnion([Q0])});
            skLineSegment(sketch, "E37.bottom", {"start": v(-3910.97, -1168.4) * mm, "end": v(-2996.57, -1168.4) * mm});
            skLineSegment(sketch, "E37.top", {"start": v(-3910.97, -1143) * mm, "end": v(-2996.57, -1143) * mm});
            skLineSegment(sketch, "E37.left", {"start": v(-3910.97, -1168.4) * mm, "end": v(-3910.97, -1143) * mm});
            skLineSegment(sketch, "E37.right", {"start": v(-2996.57, -1168.4) * mm, "end": v(-2996.57, -1143) * mm});
            skSolve(sketch);
        }
        {
            var Q0;
            Q0 = qSketchRegion(id + "F24", true);
            extrude(context, id + "F25", {"entities" : qUnion([Q0]), "operationType" : NewBodyOperationType.ADD, "oppositeDirection" : true, "depth" : 279.4 * mm, "offsetDistance" : 25.4 * mm});
        }
        {
            var Q0;
            Q0=makeQuery(id+"F25.opExtrude","SWEPT_FACE",FACE,{"disambiguationData":[OSD([sQuery(id+"F24.wireOp",EDGE,"E37.top")])]});
            var sketch = newSketch(context, id + "F26", { "sketchPlane" : qUnion([Q0])});
            skLineSegment(sketch, "E38.bottom", {"start": v(-3910.97, 457.2) * mm, "end": v(-2996.57, 457.2) * mm});
            skLineSegment(sketch, "E38.top", {"start": v(-3910.97, 431.8) * mm, "end": v(-2996.57, 431.8) * mm});
            skLineSegment(sketch, "E38.left", {"start": v(-3910.97, 457.2) * mm, "end": v(-3910.97, 431.8) * mm});
            skLineSegment(sketch, "E38.right", {"start": v(-2996.57, 457.2) * mm, "end": v(-2996.57, 431.8) * mm});
            skSolve(sketch);
        }
        {
            var Q0;
            Q0 = qSketchRegion(id + "F26", true);
            extrude(context, id + "F27", {"entities" : qUnion([Q0]), "operationType" : NewBodyOperationType.ADD, "oppositeDirection" : true, "depth" : 215.9 * mm, "offsetDistance" : 25.4 * mm});
        }
        {
            var Q0;
            Q0=makeQuery(id+"F27.opExtrude","SWEPT_FACE",FACE,{"disambiguationData":[OSD([sQuery(id+"F26.wireOp",EDGE,"E38.top")])]});
            var sketch = newSketch(context, id + "F28", { "sketchPlane" : qUnion([Q0])});
            skLineSegment(sketch, "E39.bottom", {"start": v(-3910.97, -1358.9) * mm, "end": v(-2996.57, -1358.9) * mm});
            skLineSegment(sketch, "E39.top", {"start": v(-3910.97, -1333.5) * mm, "end": v(-2996.57, -1333.5) * mm});
            skLineSegment(sketch, "E39.left", {"start": v(-3910.97, -1358.9) * mm, "end": v(-3910.97, -1333.5) * mm});
            skLineSegment(sketch, "E39.right", {"start": v(-2996.57, -1358.9) * mm, "end": v(-2996.57, -1333.5) * mm});
            skSolve(sketch);
        }
        {
            var Q0;
            Q0 = qSketchRegion(id + "F28", true);
            extrude(context, id + "F29", {"entities" : qUnion([Q0]), "operationType" : NewBodyOperationType.ADD, "oppositeDirection" : true, "depth" : 279.4 * mm, "offsetDistance" : 25.4 * mm});
        }
        {
            var Q0;
            Q0=makeQuery(id+"F29.opExtrude","SWEPT_FACE",FACE,{"disambiguationData":[OSD([sQuery(id+"F28.wireOp",EDGE,"E39.top")])]});
            var sketch = newSketch(context, id + "F30", { "sketchPlane" : qUnion([Q0])});
            skLineSegment(sketch, "E40.bottom", {"start": v(-3910.97, 711.2) * mm, "end": v(-2996.57, 711.2) * mm});
            skLineSegment(sketch, "E40.top", {"start": v(-3910.97, 685.8) * mm, "end": v(-2996.57, 685.8) * mm});
            skLineSegment(sketch, "E40.left", {"start": v(-3910.97, 711.2) * mm, "end": v(-3910.97, 685.8) * mm});
            skLineSegment(sketch, "E40.right", {"start": v(-2996.57, 711.2) * mm, "end": v(-2996.57, 685.8) * mm});
            skSolve(sketch);
        }
        {
            var Q0;
            Q0 = qSketchRegion(id + "F30", true);
            extrude(context, id + "F31", {"entities" : qUnion([Q0]), "operationType" : NewBodyOperationType.ADD, "oppositeDirection" : true, "depth" : 215.9 * mm, "offsetDistance" : 25.4 * mm});
        }
        {
            var Q0;
            Q0=makeQuery(id+"F31.opExtrude","SWEPT_FACE",FACE,{"disambiguationData":[OSD([sQuery(id+"F30.wireOp",EDGE,"E40.top")])]});
            var sketch = newSketch(context, id + "F32", { "sketchPlane" : qUnion([Q0])});
            skLineSegment(sketch, "E41.bottom", {"start": v(-3910.97, -1549.4) * mm, "end": v(-2996.57, -1549.4) * mm});
            skLineSegment(sketch, "E41.top", {"start": v(-3910.97, -1524) * mm, "end": v(-2996.57, -1524) * mm});
            skLineSegment(sketch, "E41.left", {"start": v(-3910.97, -1549.4) * mm, "end": v(-3910.97, -1524) * mm});
            skLineSegment(sketch, "E41.right", {"start": v(-2996.57, -1549.4) * mm, "end": v(-2996.57, -1524) * mm});
            skSolve(sketch);
        }
        {
            var Q0;
            Q0 = qSketchRegion(id + "F32", true);
            extrude(context, id + "F33", {"entities" : qUnion([Q0]), "operationType" : NewBodyOperationType.ADD, "oppositeDirection" : true, "depth" : 279.4 * mm, "offsetDistance" : 25.4 * mm});
        }
        {
            var Q0;
            Q0=makeQuery(id+"F33.opExtrude","SWEPT_FACE",FACE,{"disambiguationData":[OSD([sQuery(id+"F32.wireOp",EDGE,"E41.top")])]});
            var sketch = newSketch(context, id + "F34", { "sketchPlane" : qUnion([Q0])});
            skLineSegment(sketch, "E42.bottom", {"start": v(-3910.97, 965.2) * mm, "end": v(-2996.57, 965.2) * mm});
            skLineSegment(sketch, "E42.top", {"start": v(-3910.97, 939.8) * mm, "end": v(-2996.57, 939.8) * mm});
            skLineSegment(sketch, "E42.left", {"start": v(-3910.97, 965.2) * mm, "end": v(-3910.97, 939.8) * mm});
            skLineSegment(sketch, "E42.right", {"start": v(-2996.57, 965.2) * mm, "end": v(-2996.57, 939.8) * mm});
            skSolve(sketch);
        }
        {
            var Q0;
            Q0 = qSketchRegion(id + "F34", true);
            extrude(context, id + "F35", {"entities" : qUnion([Q0]), "operationType" : NewBodyOperationType.ADD, "oppositeDirection" : true, "depth" : 215.9 * mm, "offsetDistance" : 25.4 * mm});
        }
        {
            var Q0;
            Q0=makeQuery(id+"F35.opExtrude","SWEPT_FACE",FACE,{"disambiguationData":[OSD([sQuery(id+"F34.wireOp",EDGE,"E42.top")])]});
            var sketch = newSketch(context, id + "F36", { "sketchPlane" : qUnion([Q0])});
            skLineSegment(sketch, "E43.bottom", {"start": v(-3910.97, -1739.9) * mm, "end": v(-2996.57, -1739.9) * mm});
            skLineSegment(sketch, "E43.top", {"start": v(-3910.97, -1714.5) * mm, "end": v(-2996.57, -1714.5) * mm});
            skLineSegment(sketch, "E43.left", {"start": v(-3910.97, -1739.9) * mm, "end": v(-3910.97, -1714.5) * mm});
            skLineSegment(sketch, "E43.right", {"start": v(-2996.57, -1739.9) * mm, "end": v(-2996.57, -1714.5) * mm});
            skSolve(sketch);
        }
        {
            var Q0;
            Q0 = qSketchRegion(id + "F36", true);
            extrude(context, id + "F37", {"entities" : qUnion([Q0]), "operationType" : NewBodyOperationType.ADD, "oppositeDirection" : true, "depth" : 279.4 * mm, "offsetDistance" : 25.4 * mm});
        }
        {
            var Q0;
            Q0=makeQuery(id+"F37.opExtrude","SWEPT_FACE",FACE,{"disambiguationData":[OSD([sQuery(id+"F36.wireOp",EDGE,"E43.top")])]});
            var sketch = newSketch(context, id + "F38", { "sketchPlane" : qUnion([Q0])});
            skLineSegment(sketch, "E44.bottom", {"start": v(-3910.97, 1219.2) * mm, "end": v(-2996.57, 1219.2) * mm});
            skLineSegment(sketch, "E44.top", {"start": v(-3910.97, 1193.8) * mm, "end": v(-2996.57, 1193.8) * mm});
            skLineSegment(sketch, "E44.left", {"start": v(-3910.97, 1219.2) * mm, "end": v(-3910.97, 1193.8) * mm});
            skLineSegment(sketch, "E44.right", {"start": v(-2996.57, 1219.2) * mm, "end": v(-2996.57, 1193.8) * mm});
            skSolve(sketch);
        }
        {
            var Q0;
            Q0 = qSketchRegion(id + "F38", true);
            extrude(context, id + "F39", {"entities" : qUnion([Q0]), "operationType" : NewBodyOperationType.ADD, "oppositeDirection" : true, "depth" : 215.9 * mm, "offsetDistance" : 25.4 * mm});
        }
        {
            var Q0;
            Q0=makeQuery(id+"F39.opExtrude","SWEPT_FACE",FACE,{"disambiguationData":[OSD([sQuery(id+"F38.wireOp",EDGE,"E44.top")])]});
            var sketch = newSketch(context, id + "F40", { "sketchPlane" : qUnion([Q0])});
            skLineSegment(sketch, "E45.bottom", {"start": v(-3910.97, -1930.4) * mm, "end": v(-2996.57, -1930.4) * mm});
            skLineSegment(sketch, "E45.top", {"start": v(-3910.97, -1905) * mm, "end": v(-2996.57, -1905) * mm});
            skLineSegment(sketch, "E45.left", {"start": v(-3910.97, -1930.4) * mm, "end": v(-3910.97, -1905) * mm});
            skLineSegment(sketch, "E45.right", {"start": v(-2996.57, -1930.4) * mm, "end": v(-2996.57, -1905) * mm});
            skSolve(sketch);
        }
        {
            var Q0;
            Q0 = qSketchRegion(id + "F40", true);
            extrude(context, id + "F41", {"entities" : qUnion([Q0]), "operationType" : NewBodyOperationType.ADD, "oppositeDirection" : true, "depth" : 279.4 * mm, "offsetDistance" : 25.4 * mm});
        }
        {
            var Q0;
            Q0=makeQuery(id+"F41.opExtrude","SWEPT_FACE",FACE,{"disambiguationData":[OSD([sQuery(id+"F40.wireOp",EDGE,"E45.top")])]});
            var sketch = newSketch(context, id + "F42", { "sketchPlane" : qUnion([Q0])});
            skLineSegment(sketch, "E46.bottom", {"start": v(-2996.57, 1473.2) * mm, "end": v(-3910.97, 1473.2) * mm});
            skLineSegment(sketch, "E46.top", {"start": v(-2996.57, 1447.8) * mm, "end": v(-3910.97, 1447.8) * mm});
            skLineSegment(sketch, "E46.left", {"start": v(-2996.57, 1473.2) * mm, "end": v(-2996.57, 1447.8) * mm});
            skLineSegment(sketch, "E46.right", {"start": v(-3910.97, 1473.2) * mm, "end": v(-3910.97, 1447.8) * mm});
            skSolve(sketch);
        }
        {
            var Q0;
            Q0 = qSketchRegion(id + "F42", true);
            extrude(context, id + "F43", {"entities" : qUnion([Q0]), "operationType" : NewBodyOperationType.ADD, "oppositeDirection" : true, "depth" : 215.9 * mm, "offsetDistance" : 25.4 * mm});
        }
        {
            var Q0;
            Q0=makeQuery(id+"F43.opExtrude","SWEPT_FACE",FACE,{"disambiguationData":[OSD([sQuery(id+"F42.wireOp",EDGE,"E46.top")])]});
            var sketch = newSketch(context, id + "F44", { "sketchPlane" : qUnion([Q0])});
            skLineSegment(sketch, "E47.bottom", {"start": v(-3910.97, -2120.9) * mm, "end": v(-2996.57, -2120.9) * mm});
            skLineSegment(sketch, "E47.top", {"start": v(-3910.97, -2095.5) * mm, "end": v(-2996.57, -2095.5) * mm});
            skLineSegment(sketch, "E47.left", {"start": v(-3910.97, -2120.9) * mm, "end": v(-3910.97, -2095.5) * mm});
            skLineSegment(sketch, "E47.right", {"start": v(-2996.57, -2120.9) * mm, "end": v(-2996.57, -2095.5) * mm});
            skSolve(sketch);
        }
        {
            var Q0;
            Q0 = qSketchRegion(id + "F44", true);
            extrude(context, id + "F45", {"entities" : qUnion([Q0]), "operationType" : NewBodyOperationType.ADD, "oppositeDirection" : true, "depth" : 279.4 * mm, "offsetDistance" : 25.4 * mm});
        }
        {
            var Q0;
            Q0=makeQuery(id+"F45.opExtrude","SWEPT_FACE",FACE,{"disambiguationData":[OSD([sQuery(id+"F44.wireOp",EDGE,"E47.top")])]});
            var sketch = newSketch(context, id + "F46", { "sketchPlane" : qUnion([Q0])});
            skLineSegment(sketch, "E48.bottom", {"start": v(-2996.57, 1727.2) * mm, "end": v(-3910.97, 1727.2) * mm});
            skLineSegment(sketch, "E48.top", {"start": v(-2996.57, 1701.8) * mm, "end": v(-3910.97, 1701.8) * mm});
            skLineSegment(sketch, "E48.left", {"start": v(-2996.57, 1727.2) * mm, "end": v(-2996.57, 1701.8) * mm});
            skLineSegment(sketch, "E48.right", {"start": v(-3910.97, 1727.2) * mm, "end": v(-3910.97, 1701.8) * mm});
            skSolve(sketch);
        }
        {
            var Q0;
            Q0 = qSketchRegion(id + "F46", true);
            extrude(context, id + "F47", {"entities" : qUnion([Q0]), "operationType" : NewBodyOperationType.ADD, "oppositeDirection" : true, "depth" : 215.9 * mm, "offsetDistance" : 25.4 * mm});
        }
        {
            var Q0;
            Q0=makeQuery(id+"F47.opExtrude","SWEPT_FACE",FACE,{"disambiguationData":[OSD([sQuery(id+"F46.wireOp",EDGE,"E48.top")])]});
            var sketch = newSketch(context, id + "F48", { "sketchPlane" : qUnion([Q0])});
            skLineSegment(sketch, "E49.bottom", {"start": v(-3910.97, -2311.4) * mm, "end": v(-2996.57, -2311.4) * mm});
            skLineSegment(sketch, "E49.top", {"start": v(-3910.97, -2286) * mm, "end": v(-2996.57, -2286) * mm});
            skLineSegment(sketch, "E49.left", {"start": v(-3910.97, -2311.4) * mm, "end": v(-3910.97, -2286) * mm});
            skLineSegment(sketch, "E49.right", {"start": v(-2996.57, -2311.4) * mm, "end": v(-2996.57, -2286) * mm});
            skSolve(sketch);
        }
        {
            var Q0;
            Q0 = qSketchRegion(id + "F48", true);
            extrude(context, id + "F49", {"entities" : qUnion([Q0]), "operationType" : NewBodyOperationType.ADD, "oppositeDirection" : true, "depth" : 279.4 * mm, "offsetDistance" : 25.4 * mm});
        }
        {
            var Q0;
            Q0=makeQuery(id+"F49.opExtrude","SWEPT_FACE",FACE,{"disambiguationData":[OSD([sQuery(id+"F48.wireOp",EDGE,"E49.top")])]});
            var sketch = newSketch(context, id + "F50", { "sketchPlane" : qUnion([Q0])});
            skLineSegment(sketch, "E50.bottom", {"start": v(-2996.57, 1981.2) * mm, "end": v(-3910.97, 1981.2) * mm});
            skLineSegment(sketch, "E50.top", {"start": v(-2996.57, 1955.8) * mm, "end": v(-3910.97, 1955.8) * mm});
            skLineSegment(sketch, "E50.left", {"start": v(-2996.57, 1981.2) * mm, "end": v(-2996.57, 1955.8) * mm});
            skLineSegment(sketch, "E50.right", {"start": v(-3910.97, 1981.2) * mm, "end": v(-3910.97, 1955.8) * mm});
            skSolve(sketch);
        }
        {
            var Q0;
            Q0 = qSketchRegion(id + "F50", true);
            extrude(context, id + "F51", {"entities" : qUnion([Q0]), "operationType" : NewBodyOperationType.ADD, "oppositeDirection" : true, "depth" : 215.9 * mm, "offsetDistance" : 25.4 * mm});
        }
        {
            var Q0;
            Q0=makeQuery(id+"F1.opExtrude","CAP_FACE",FACE,{"disambiguationData":[OSD([sQuery(id+"F0.wireOp",EDGE,"E0.bottom"),sQuery(id+"F0.wireOp",EDGE,"E0.top"),sQuery(id+"F0.wireOp",EDGE,"E0.left"),sQuery(id+"F0.wireOp",EDGE,"E1.bottom"),sQuery(id+"F0.wireOp",EDGE,"E1.top"),sQuery(id+"F0.wireOp",EDGE,"E1.left"),sQuery(id+"F0.wireOp",EDGE,"E1.right"),sQuery(id+"F0.wireOp",EDGE,"E2.bottom"),sQuery(id+"F0.wireOp",EDGE,"E3.bottom"),sQuery(id+"F0.wireOp",EDGE,"E4.top"),sQuery(id+"F0.wireOp",EDGE,"E4.right"),sQuery(id+"F0.wireOp",EDGE,"E5.bottom"),sQuery(id+"F0.wireOp",EDGE,"E5.top"),sQuery(id+"F0.wireOp",EDGE,"E5.left"),sQuery(id+"F0.wireOp",EDGE,"E5.right"),sQuery(id+"F0.wireOp",EDGE,"E6.bottom"),sQuery(id+"F0.wireOp",EDGE,"E7.bottom"),sQuery(id+"F0.wireOp",EDGE,"E8.top"),sQuery(id+"F0.wireOp",EDGE,"E8.right"),sQuery(id+"F0.wireOp",EDGE,"E9.bottom"),sQuery(id+"F0.wireOp",EDGE,"E9.top"),sQuery(id+"F0.wireOp",EDGE,"E9.left"),sQuery(id+"F0.wireOp",EDGE,"E9.right"),sQuery(id+"F0.wireOp",EDGE,"E10"),sQuery(id+"F0.wireOp",EDGE,"E11"),sQuery(id+"F0.wireOp",EDGE,"E12"),sQuery(id+"F0.wireOp",EDGE,"E13.bottom"),sQuery(id+"F0.wireOp",EDGE,"E13.top"),sQuery(id+"F0.wireOp",EDGE,"E13.left"),sQuery(id+"F0.wireOp",EDGE,"E13.right"),sQuery(id+"F0.wireOp",EDGE,"E14.top"),sQuery(id+"F0.wireOp",EDGE,"E14.right"),sQuery(id+"F0.wireOp",EDGE,"E15.bottom"),sQuery(id+"F0.wireOp",EDGE,"E15.top"),sQuery(id+"F0.wireOp",EDGE,"E15.left"),sQuery(id+"F0.wireOp",EDGE,"E15.right"),sQuery(id+"F0.wireOp",EDGE,"E16.bottom"),sQuery(id+"F0.wireOp",EDGE,"E16.top"),sQuery(id+"F0.wireOp",EDGE,"E16.right"),sQuery(id+"F0.wireOp",EDGE,"E17.bottom"),sQuery(id+"F0.wireOp",EDGE,"E17.top"),sQuery(id+"F0.wireOp",EDGE,"E17.left"),sQuery(id+"F0.wireOp",EDGE,"E17.right"),sQuery(id+"F0.wireOp",EDGE,"E18.bottom"),sQuery(id+"F0.wireOp",EDGE,"E18.top"),sQuery(id+"F0.wireOp",EDGE,"E19.left"),sQuery(id+"F0.wireOp",EDGE,"E20.bottom"),sQuery(id+"F0.wireOp",EDGE,"E20.top"),sQuery(id+"F0.wireOp",EDGE,"E20.left"),sQuery(id+"F0.wireOp",EDGE,"E21.top"),sQuery(id+"F0.wireOp",EDGE,"E21.left"),sQuery(id+"F0.wireOp",EDGE,"E21.right")])],"isStart":false});
            var sketch = newSketch(context, id + "F52", { "sketchPlane" : qUnion([Q0])});
            skLineSegment(sketch, "E51.bottom", {"start": v(-1878.97, -1955.8) * mm, "end": v(-2793.37, -1955.8) * mm});
            skLineSegment(sketch, "E51.top", {"start": v(-1878.97, -1930.4) * mm, "end": v(-2793.37, -1930.4) * mm});
            skLineSegment(sketch, "E51.left", {"start": v(-1878.97, -1955.8) * mm, "end": v(-1878.97, -1930.4) * mm});
            skLineSegment(sketch, "E51.right", {"start": v(-2793.37, -1955.8) * mm, "end": v(-2793.37, -1930.4) * mm});
            skSolve(sketch);
        }
        {
            var Q0;
            Q0 = qSketchRegion(id + "F52", true);
            extrude(context, id + "F53", {"entities" : qUnion([Q0]), "operationType" : NewBodyOperationType.ADD, "oppositeDirection" : true, "depth" : 241.3 * mm, "offsetDistance" : 25.4 * mm});
        }
        {
            var Q0;
            Q0=makeQuery(id+"F53.opExtrude","SWEPT_FACE",FACE,{"disambiguationData":[OSD([sQuery(id+"F52.wireOp",EDGE,"E51.top")])]});
            var sketch = newSketch(context, id + "F54", { "sketchPlane" : qUnion([Q0])});
            skLineSegment(sketch, "E52.bottom", {"start": v(-2793.37, 215.9) * mm, "end": v(-1878.97, 215.9) * mm});
            skLineSegment(sketch, "E52.top", {"start": v(-2793.37, 190.5) * mm, "end": v(-1878.97, 190.5) * mm});
            skLineSegment(sketch, "E52.left", {"start": v(-2793.37, 215.9) * mm, "end": v(-2793.37, 190.5) * mm});
            skLineSegment(sketch, "E52.right", {"start": v(-1878.97, 215.9) * mm, "end": v(-1878.97, 190.5) * mm});
            skSolve(sketch);
        }
        {
            var Q0;
            Q0 = qSketchRegion(id + "F54", true);
            extrude(context, id + "F55", {"entities" : qUnion([Q0]), "operationType" : NewBodyOperationType.ADD, "oppositeDirection" : true, "depth" : 279.4 * mm, "offsetDistance" : 25.4 * mm});
        }
        {
            var Q0;
            Q0=makeQuery(id+"F55.opExtrude","SWEPT_FACE",FACE,{"disambiguationData":[OSD([sQuery(id+"F54.wireOp",EDGE,"E52.top")])]});
            var sketch = newSketch(context, id + "F56", { "sketchPlane" : qUnion([Q0])});
            skLineSegment(sketch, "E53.bottom", {"start": v(-1878.97, -2209.8) * mm, "end": v(-2793.37, -2209.8) * mm});
            skLineSegment(sketch, "E53.top", {"start": v(-1878.97, -2184.4) * mm, "end": v(-2793.37, -2184.4) * mm});
            skLineSegment(sketch, "E53.left", {"start": v(-1878.97, -2209.8) * mm, "end": v(-1878.97, -2184.4) * mm});
            skLineSegment(sketch, "E53.right", {"start": v(-2793.37, -2209.8) * mm, "end": v(-2793.37, -2184.4) * mm});
            skSolve(sketch);
        }
        {
            var Q0;
            Q0 = qSketchRegion(id + "F56", true);
            extrude(context, id + "F57", {"entities" : qUnion([Q0]), "operationType" : NewBodyOperationType.ADD, "oppositeDirection" : true, "depth" : 241.3 * mm, "offsetDistance" : 25.4 * mm});
        }
        {
            var Q0;
            Q0=makeQuery(id+"F57.opExtrude","SWEPT_FACE",FACE,{"disambiguationData":[OSD([sQuery(id+"F56.wireOp",EDGE,"E53.top")])]});
            var sketch = newSketch(context, id + "F58", { "sketchPlane" : qUnion([Q0])});
            skLineSegment(sketch, "E54.bottom", {"start": v(-2793.37, 431.8) * mm, "end": v(-1878.97, 431.8) * mm});
            skLineSegment(sketch, "E54.top", {"start": v(-2793.37, 406.4) * mm, "end": v(-1878.97, 406.4) * mm});
            skLineSegment(sketch, "E54.left", {"start": v(-2793.37, 431.8) * mm, "end": v(-2793.37, 406.4) * mm});
            skLineSegment(sketch, "E54.right", {"start": v(-1878.97, 431.8) * mm, "end": v(-1878.97, 406.4) * mm});
            skSolve(sketch);
        }
        {
            var Q0;
            Q0 = qSketchRegion(id + "F58", true);
            extrude(context, id + "F59", {"entities" : qUnion([Q0]), "operationType" : NewBodyOperationType.ADD, "oppositeDirection" : true, "depth" : 279.4 * mm, "offsetDistance" : 25.4 * mm});
        }
        {
            var Q0;
            Q0=makeQuery(id+"F59.opExtrude","SWEPT_FACE",FACE,{"disambiguationData":[OSD([sQuery(id+"F58.wireOp",EDGE,"E54.top")])]});
            var sketch = newSketch(context, id + "F60", { "sketchPlane" : qUnion([Q0])});
            skLineSegment(sketch, "E55.bottom", {"start": v(-1878.97, -2463.8) * mm, "end": v(-2793.37, -2463.8) * mm});
            skLineSegment(sketch, "E55.top", {"start": v(-1878.97, -2438.4) * mm, "end": v(-2793.37, -2438.4) * mm});
            skLineSegment(sketch, "E55.left", {"start": v(-1878.97, -2463.8) * mm, "end": v(-1878.97, -2438.4) * mm});
            skLineSegment(sketch, "E55.right", {"start": v(-2793.37, -2463.8) * mm, "end": v(-2793.37, -2438.4) * mm});
            skSolve(sketch);
        }
        {
            var Q0;
            Q0 = qSketchRegion(id + "F60", true);
            extrude(context, id + "F61", {"entities" : qUnion([Q0]), "operationType" : NewBodyOperationType.ADD, "oppositeDirection" : true, "depth" : 241.3 * mm, "offsetDistance" : 25.4 * mm});
        }
        {
            var Q0;
            Q0=makeQuery(id+"F61.opExtrude","SWEPT_FACE",FACE,{"disambiguationData":[OSD([sQuery(id+"F60.wireOp",EDGE,"E55.top")])]});
            var sketch = newSketch(context, id + "F62", { "sketchPlane" : qUnion([Q0])});
            skLineSegment(sketch, "E56.bottom", {"start": v(-2793.37, 647.7) * mm, "end": v(-1878.97, 647.7) * mm});
            skLineSegment(sketch, "E56.top", {"start": v(-2793.37, 622.3) * mm, "end": v(-1878.97, 622.3) * mm});
            skLineSegment(sketch, "E56.left", {"start": v(-2793.37, 647.7) * mm, "end": v(-2793.37, 622.3) * mm});
            skLineSegment(sketch, "E56.right", {"start": v(-1878.97, 647.7) * mm, "end": v(-1878.97, 622.3) * mm});
            skSolve(sketch);
        }
        {
            var Q0;
            Q0 = qSketchRegion(id + "F62", true);
            extrude(context, id + "F63", {"entities" : qUnion([Q0]), "operationType" : NewBodyOperationType.ADD, "oppositeDirection" : true, "depth" : 279.4 * mm, "offsetDistance" : 25.4 * mm});
        }
        {
            var Q0;
            Q0=makeQuery(id+"F63.opExtrude","SWEPT_FACE",FACE,{"disambiguationData":[OSD([sQuery(id+"F62.wireOp",EDGE,"E56.top")])]});
            var sketch = newSketch(context, id + "F64", { "sketchPlane" : qUnion([Q0])});
            skLineSegment(sketch, "E57.bottom", {"start": v(-1878.97, -2717.8) * mm, "end": v(-2793.37, -2717.8) * mm});
            skLineSegment(sketch, "E57.top", {"start": v(-1878.97, -2692.4) * mm, "end": v(-2793.37, -2692.4) * mm});
            skLineSegment(sketch, "E57.left", {"start": v(-1878.97, -2717.8) * mm, "end": v(-1878.97, -2692.4) * mm});
            skLineSegment(sketch, "E57.right", {"start": v(-2793.37, -2717.8) * mm, "end": v(-2793.37, -2692.4) * mm});
            skSolve(sketch);
        }
        {
            var Q0;
            Q0 = qSketchRegion(id + "F64", true);
            extrude(context, id + "F65", {"entities" : qUnion([Q0]), "operationType" : NewBodyOperationType.ADD, "oppositeDirection" : true, "depth" : 241.3 * mm, "offsetDistance" : 25.4 * mm});
        }
        {
            var Q0;
            Q0=makeQuery(id+"F65.opExtrude","SWEPT_FACE",FACE,{"disambiguationData":[OSD([sQuery(id+"F64.wireOp",EDGE,"E57.top")])]});
            var sketch = newSketch(context, id + "F66", { "sketchPlane" : qUnion([Q0])});
            skLineSegment(sketch, "E58.bottom", {"start": v(-2793.37, 863.6) * mm, "end": v(-1878.97, 863.6) * mm});
            skLineSegment(sketch, "E58.top", {"start": v(-2793.37, 838.2) * mm, "end": v(-1878.97, 838.2) * mm});
            skLineSegment(sketch, "E58.left", {"start": v(-2793.37, 863.6) * mm, "end": v(-2793.37, 838.2) * mm});
            skLineSegment(sketch, "E58.right", {"start": v(-1878.97, 863.6) * mm, "end": v(-1878.97, 838.2) * mm});
            skSolve(sketch);
        }
        {
            var Q0;
            Q0 = qSketchRegion(id + "F66", true);
            extrude(context, id + "F67", {"entities" : qUnion([Q0]), "operationType" : NewBodyOperationType.ADD, "oppositeDirection" : true, "depth" : 279.4 * mm, "offsetDistance" : 25.4 * mm});
        }
        {
            var Q0;
            Q0=makeQuery(id+"F67.opExtrude","SWEPT_FACE",FACE,{"disambiguationData":[OSD([sQuery(id+"F66.wireOp",EDGE,"E58.top")])]});
            var sketch = newSketch(context, id + "F68", { "sketchPlane" : qUnion([Q0])});
            skLineSegment(sketch, "E59.bottom", {"start": v(-1878.97, -2971.8) * mm, "end": v(-2793.37, -2971.8) * mm});
            skLineSegment(sketch, "E59.top", {"start": v(-1878.97, -2946.4) * mm, "end": v(-2793.37, -2946.4) * mm});
            skLineSegment(sketch, "E59.left", {"start": v(-1878.97, -2971.8) * mm, "end": v(-1878.97, -2946.4) * mm});
            skLineSegment(sketch, "E59.right", {"start": v(-2793.37, -2971.8) * mm, "end": v(-2793.37, -2946.4) * mm});
            skSolve(sketch);
        }
        {
            var Q0;
            Q0 = qSketchRegion(id + "F68", true);
            extrude(context, id + "F69", {"entities" : qUnion([Q0]), "operationType" : NewBodyOperationType.ADD, "oppositeDirection" : true, "depth" : 241.3 * mm, "offsetDistance" : 25.4 * mm});
        }
        {
            var Q0;
            Q0=makeQuery(id+"F69.opExtrude","SWEPT_FACE",FACE,{"disambiguationData":[OSD([sQuery(id+"F68.wireOp",EDGE,"E59.top")])]});
            var sketch = newSketch(context, id + "F70", { "sketchPlane" : qUnion([Q0])});
            skLineSegment(sketch, "E60.bottom", {"start": v(-2793.37, 1079.5) * mm, "end": v(-1878.97, 1079.5) * mm});
            skLineSegment(sketch, "E60.top", {"start": v(-2793.37, 1054.1) * mm, "end": v(-1878.97, 1054.1) * mm});
            skLineSegment(sketch, "E60.left", {"start": v(-2793.37, 1079.5) * mm, "end": v(-2793.37, 1054.1) * mm});
            skLineSegment(sketch, "E60.right", {"start": v(-1878.97, 1079.5) * mm, "end": v(-1878.97, 1054.1) * mm});
            skSolve(sketch);
        }
        {
            var Q0;
            Q0 = qSketchRegion(id + "F70", true);
            extrude(context, id + "F71", {"entities" : qUnion([Q0]), "operationType" : NewBodyOperationType.ADD, "oppositeDirection" : true, "depth" : 279.4 * mm, "offsetDistance" : 25.4 * mm});
        }
    });
